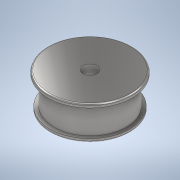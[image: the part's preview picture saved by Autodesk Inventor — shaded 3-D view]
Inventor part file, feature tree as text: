
AUTODESK INVENTOR PART (.ipt)
format: ipt  version: 2022 (Build 260153000, 153)  size: 145,920 bytes
history: native  units: in
note: dims shown in document units (in); Inventor stores cm internally (conversion verified against a paired STEP export)
features: revolve x1, sketch x1
ambient origin geometry x8: Origin, YZ Plane, XZ Plane, XY Plane, X Axis, Y Axis, Z Axis, Center Point
bodies: Solid1 (feature_tree)
feature tree (2):
  revolve  "Revolution1"  [1 undecoded]
  sketch  "Sketch1"  dims[d0=1.9685in d1=0.3937in d2=1.9685in d3=0.1969in d4=0.315in d5=1.5748in d6=0.1969in d7=1.8504in d8=0.0787in d9=90.0deg]
note: 1 required parameter value undecoded (feature->parameter linkage not recoverable at this tier; creation-order binding heuristic only, values carry confidence <= 0.55)
